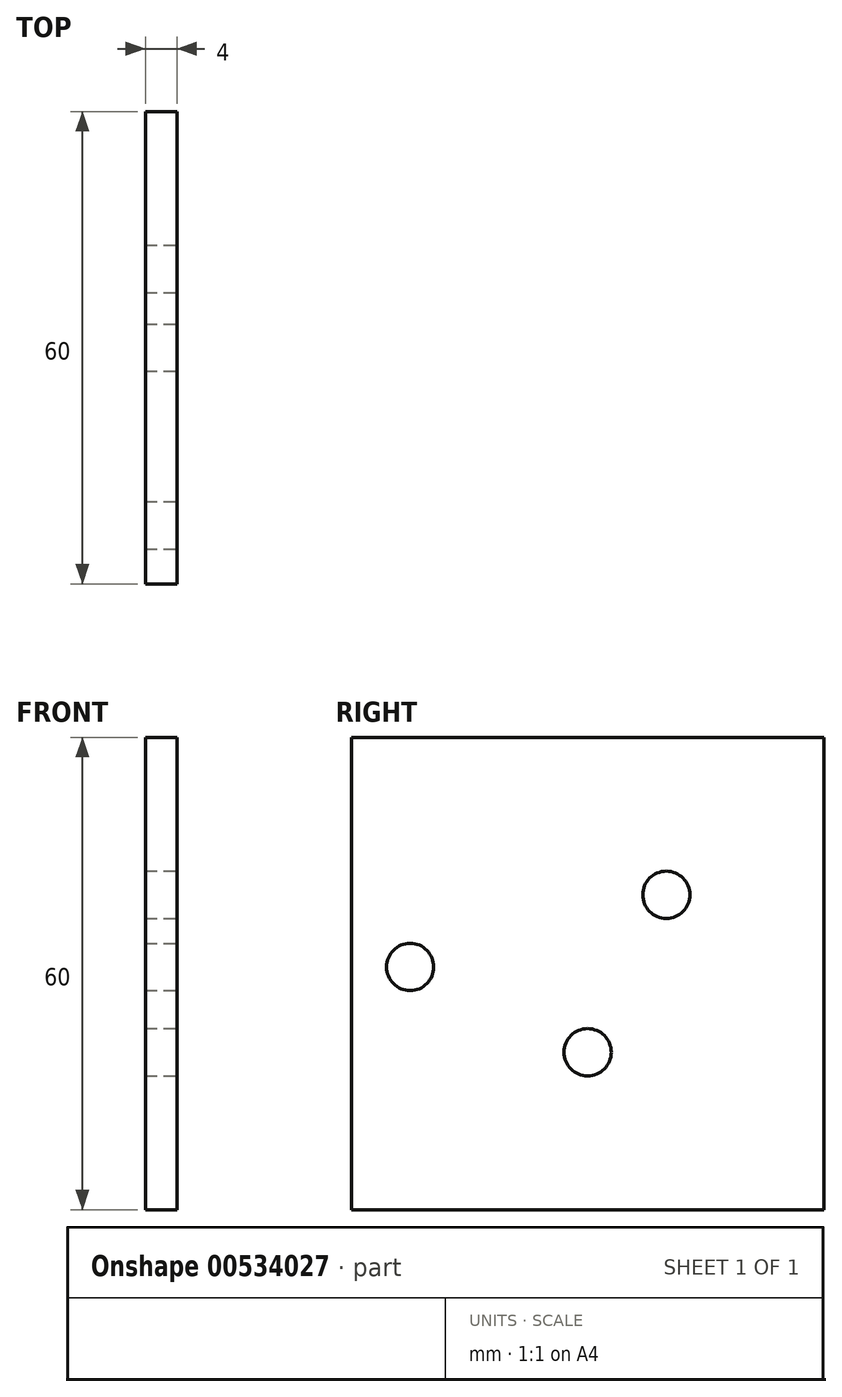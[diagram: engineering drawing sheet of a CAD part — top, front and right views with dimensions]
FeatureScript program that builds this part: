
annotation { "Feature Type Name" : "Feature", "Feature Type Description" : "" }
export const myFeature = defineFeature(function(context is Context, id is Id, definition is map)
    precondition{}
    {
        {
            var Q0;
            Q0=qCreatedBy(makeId("Right.planeOp"),FACE);
            var sketch = newSketch(context, id + "F0", { "sketchPlane" : qUnion([Q0])});
            skLineSegment(sketch, "E0.bottom", {"start": v(0, 60) * mm, "end": v(60, 60) * mm});
            skLineSegment(sketch, "E0.top", {"start": v(0, 0) * mm, "end": v(60, 0) * mm});
            skLineSegment(sketch, "E0.left", {"start": v(0, 60) * mm, "end": v(0, 0) * mm});
            skLineSegment(sketch, "E0.right", {"start": v(60, 60) * mm, "end": v(60, 0) * mm});
            skSolve(sketch);
        }
        {
            var Q0;
            Q0=makeQuery(id+"F0.imprint","IMPRINT",FACE,{"disambiguationData":[TD([[makeQuery(id+"F0.imprint","IMPRINT",EDGE,{"derivedFrom":sQuery(id+"F0.wireOp",EDGE,"E0.bottom")}),-1.0]])]});
            extrude(context, id + "F1", {"entities" : qUnion([Q0]), "depth" : 4 * mm, "offsetDistance" : 25 * mm});
        }
        {
            var Q0;
            Q0=makeQuery(id+"F1.opExtrude","CAP_FACE",FACE,{"disambiguationData":[OSD([sQuery(id+"F0.wireOp",EDGE,"E0.bottom"),sQuery(id+"F0.wireOp",EDGE,"E0.top"),sQuery(id+"F0.wireOp",EDGE,"E0.left"),sQuery(id+"F0.wireOp",EDGE,"E0.right")])],"isStart":false});
            var sketch = newSketch(context, id + "F2", { "sketchPlane" : qUnion([Q0])});
            skCircle(sketch, "E1", {"center": v(40, 40) * mm, "radius": 3 * mm});
            skCircle(sketch, "E2", {"center": v(7.45, 30.83) * mm, "radius": 3 * mm});
            skCircle(sketch, "E3", {"center": v(30, 20) * mm, "radius": 3 * mm});
            skLineSegment(sketch, "E4", {"start": v(30, 60) * mm, "end": v(30, 0) * mm, "construction": true});
            skPoint(sketch, "E4.endSnap0", {"position": v(30, 0) * mm});
            skSolve(sketch);
        }
        {
            var Q0;
            Q0 = qSketchRegion(id + "F2", true);
            extrude(context, id + "F3", {"entities" : qUnion([Q0]), "operationType" : NewBodyOperationType.REMOVE, "endBound" : BoundingType.UP_TO_NEXT, "oppositeDirection" : true, "depth" : 25 * mm, "offsetDistance" : 25 * mm});
        }
    });
